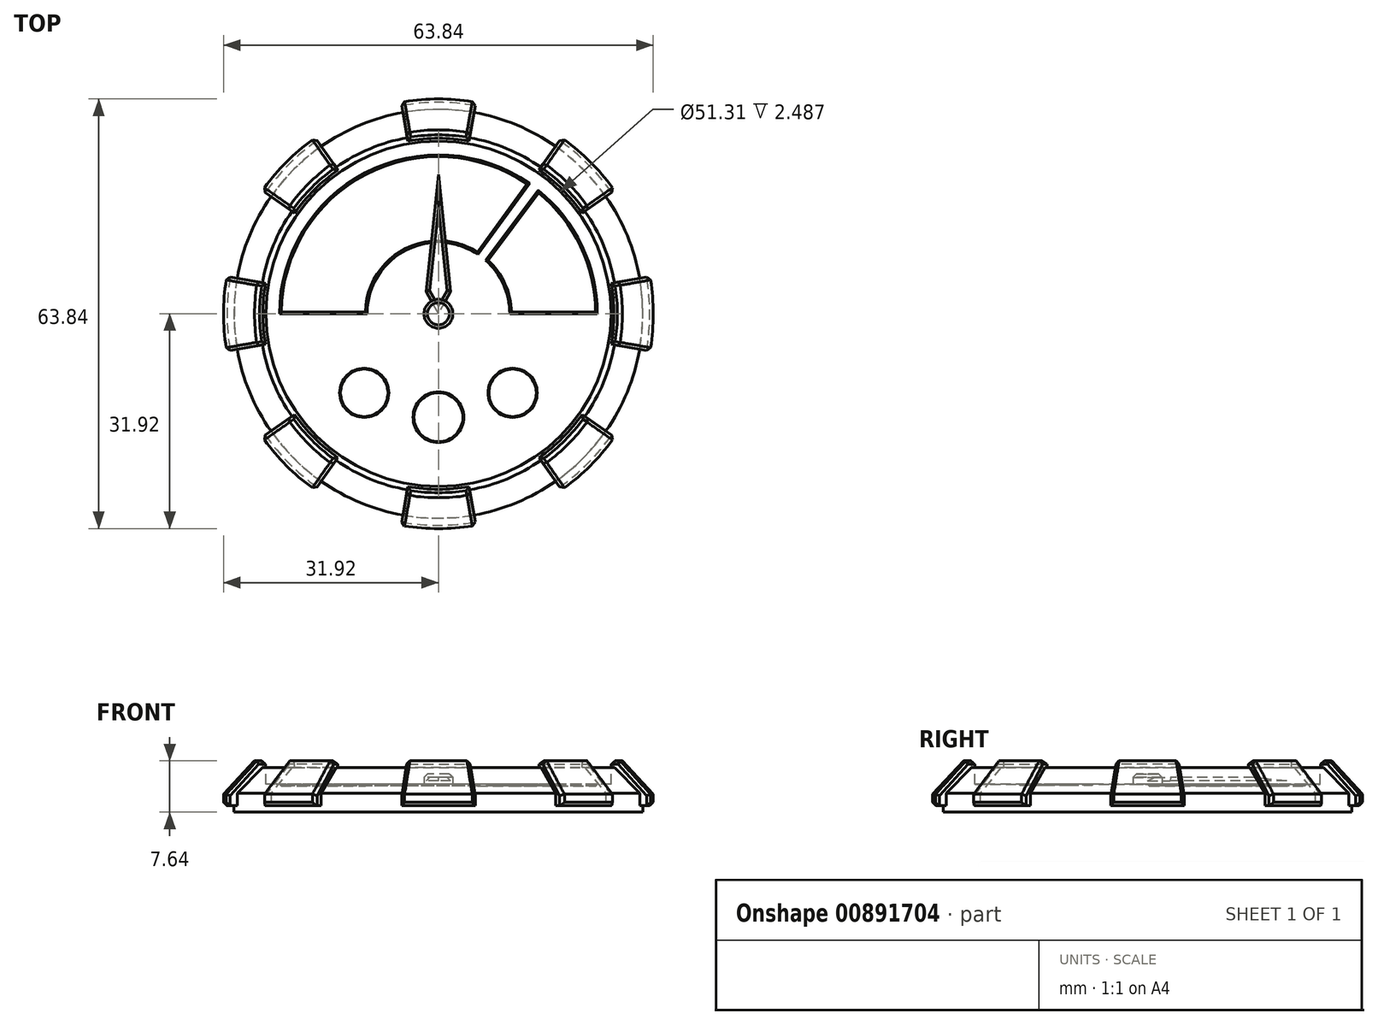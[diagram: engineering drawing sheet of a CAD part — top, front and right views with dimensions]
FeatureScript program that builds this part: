
annotation { "Feature Type Name" : "Feature", "Feature Type Description" : "" }
export const myFeature = defineFeature(function(context is Context, id is Id, definition is map)
    precondition{}
    {
        {
            var Q0;
            Q0=qCreatedBy(makeId("Top.planeOp"),FACE);
            var sketch = newSketch(context, id + "F0", { "sketchPlane" : qUnion([Q0])});
            skCircle(sketch, "E0", {"center": v(0, 0) * mm, "radius": 30.37 * mm});
            skSolve(sketch);
        }
        {
            var Q0;
            Q0 = qSketchRegion(id + "F0", true);
            extrude(context, id + "F1", {"entities" : qUnion([Q0]), "depth" : 6.65 * mm, "offsetDistance" : 25.4 * mm});
        }
        {
            var Q0;
            Q0=makeQuery(id+"F1.opExtrude","CAP_EDGE",EDGE,{"disambiguationData":[OSD([sQuery(id+"F0.wireOp",EDGE,"E0")])],"isStart":false});
            chamfer(context, id + "F2", {"entities" : qUnion([Q0]), "width" : 3.8 * mm, "tangentPropagation" : true});
        }
        {
            var Q0;
            Q0=makeQuery(id+"F1.opExtrude","CAP_FACE",FACE,{"disambiguationData":[OSD([sQuery(id+"F0.wireOp",EDGE,"E0")])],"isStart":false});
            var sketch = newSketch(context, id + "F3", { "sketchPlane" : qUnion([Q0])});
            skCircle(sketch, "E1", {"center": v(0, 0) * mm, "radius": 25.66 * mm});
            skSolve(sketch);
        }
        {
            var Q0;
            Q0 = qSketchRegion(id + "F3", true);
            extrude(context, id + "F4", {"entities" : qUnion([Q0]), "operationType" : NewBodyOperationType.REMOVE, "oppositeDirection" : true, "depth" : 2.5 * mm, "offsetDistance" : 25.4 * mm});
        }
        {
            var Q0;
            Q0=qCreatedBy(makeId("Right.planeOp"),FACE);
            var sketch = newSketch(context, id + "F5", { "sketchPlane" : qUnion([Q0])});
            skLineSegment(sketch, "E2", {"start": v(-26.08, 6.1) * mm, "end": v(-26.08, 7.63) * mm});
            skLineSegment(sketch, "E3", {"start": v(-26.08, 7.63) * mm, "end": v(-27.33, 7.63) * mm});
            skLineSegment(sketch, "E4", {"start": v(-27.33, 7.63) * mm, "end": v(-31.92, 2.66) * mm});
            skLineSegment(sketch, "E5", {"start": v(-31.92, 2.66) * mm, "end": v(-31.92, 0.95) * mm});
            skLineSegment(sketch, "E6", {"start": v(-31.92, 0.95) * mm, "end": v(-30.03, 0.95) * mm});
            skLineSegment(sketch, "E7", {"start": v(-30.03, 0.95) * mm, "end": v(-26.08, 6.1) * mm});
            skLineSegment(sketch, "E8", {"start": v(0, 11.9) * mm, "end": v(0, 0) * mm});
            skSolve(sketch);
        }
        {
            var Q0;
            Q0=makeQuery(id+"F5.imprint","IMPRINT",FACE,{"disambiguationData":[TD([[makeQuery(id+"F5.imprint","IMPRINT",EDGE,{"derivedFrom":sQuery(id+"F5.wireOp",EDGE,"E2")}),1.0]])]});
            var Q1;
            Q1=sQuery(id+"F5.wireOp",EDGE,"E8");
            revolve(context, id + "F6", {"operationType" : NewBodyOperationType.ADD, "surfaceOperationType" : NewSurfaceOperationType.NEW, "entities" : qUnion([Q0]), "axis" : qUnion([Q1]), "revolveType" : RevolveType.SYMMETRIC, "angle" : 20 * degree});
        }
        {
            var Q0;
            Q0=makeQuery(id+"F6.opRevolve","SWEPT_EDGE",EDGE,{"disambiguationData":[OSD([sQuery(id+"F5.wireOp",EDGE,"E5"),sQuery(id+"F5.wireOp",EDGE,"E6")])]});
            var Q1;
            Q1=makeQuery(id+"F6.opRevolve","CAP_EDGE",EDGE,{"disambiguationData":[OSD([sQuery(id+"F5.wireOp",EDGE,"E5")])],"isStart":false});
            var Q2;
            Q2=makeQuery(id+"F6.opRevolve","CAP_EDGE",EDGE,{"disambiguationData":[OSD([sQuery(id+"F5.wireOp",EDGE,"E4")])],"isStart":false});
            var Q3;
            Q3=makeQuery(id+"F6.opRevolve","CAP_EDGE",EDGE,{"disambiguationData":[OSD([sQuery(id+"F5.wireOp",EDGE,"E3")])],"isStart":false});
            var Q4;
            Q4=makeQuery(id+"F6.opRevolve","SWEPT_EDGE",EDGE,{"disambiguationData":[OSD([sQuery(id+"F5.wireOp",EDGE,"E2"),sQuery(id+"F5.wireOp",EDGE,"E3")])]});
            var Q5;
            Q5=makeQuery(id+"F6.opRevolve","CAP_EDGE",EDGE,{"disambiguationData":[OSD([sQuery(id+"F5.wireOp",EDGE,"E3")])],"isStart":true});
            var Q6;
            Q6=makeQuery(id+"F6.opRevolve","CAP_EDGE",EDGE,{"disambiguationData":[OSD([sQuery(id+"F5.wireOp",EDGE,"E4")])],"isStart":true});
            var Q7;
            Q7=makeQuery(id+"F6.opRevolve","CAP_EDGE",EDGE,{"disambiguationData":[OSD([sQuery(id+"F5.wireOp",EDGE,"E5")])],"isStart":true});
            chamfer(context, id + "F7", {"entities" : qUnion([Q0, Q1, Q2, Q3, Q4, Q5, Q6, Q7]), "width" : 0.5 * mm, "tangentPropagation" : true});
        }
        {
            var Q0;
            Q0=makeQuery(id+"F1.opExtrude","SWEPT_BODY",BODY,{"disambiguationData":[OSD([sQuery(id+"F0.wireOp",EDGE,"E0")])]});
            var Q1;
            Q1=sQuery(id+"F5.wireOp",EDGE,"E8");
            circularPattern(context, id + "F8", {"operationType" : NewBodyOperationType.ADD, "entities" : qUnion([Q0]), "axis" : qUnion([Q1]), "angle" : 360 * degree, "instanceCount" : 8, "equalSpace" : true});
        }
        {
            var Q0;
            Q0=makeQuery(id+"F4.boolean.opBoolean","COPY",FACE,{"derivedFrom":makeQuery(id+"F4.opExtrude","CAP_FACE",FACE,{"disambiguationData":[OSD([sQuery(id+"F3.wireOp",EDGE,"E1")])],"isStart":false})});
            var sketch = newSketch(context, id + "F9", { "sketchPlane" : qUnion([Q0])});
            skCircle(sketch, "E9", {"center": v(0, -15.36) * mm, "radius": 3.9 * mm});
            skCircle(sketch, "E10", {"center": v(11.02, -11.74) * mm, "radius": 3.78 * mm});
            skLineSegment(sketch, "E11", {"start": v(0, -8.23) * mm, "end": v(0, 0) * mm});
            skCircle(sketch, "E12.MirrorC", {"center": v(-11.02, -11.74) * mm, "radius": 3.78 * mm});
            skSolve(sketch);
        }
        {
            var Q0;
            Q0 = qSketchRegion(id + "F9", true);
            extrude(context, id + "F10", {"entities" : qUnion([Q0]), "operationType" : NewBodyOperationType.REMOVE, "oppositeDirection" : true, "depth" : 0.13 * mm, "offsetDistance" : 25.4 * mm});
        }
        {
            var Q0;
            Q0=makeQuery(id+"F4.boolean.opBoolean","COPY",FACE,{"derivedFrom":makeQuery(id+"F4.opExtrude","CAP_FACE",FACE,{"disambiguationData":[OSD([sQuery(id+"F3.wireOp",EDGE,"E1")])],"isStart":false})});
            var sketch = newSketch(context, id + "F11", { "sketchPlane" : qUnion([Q0])});
            skArc(sketch, "E13", {"start": v(23.61, 0.01) * mm, "mid": v(21.3, 10.18) * mm, "end": v(14.85, 18.36) * mm});
            skLineSegment(sketch, "E14", {"start": v(-23.61, 0.04) * mm, "end": v(-10.6, 0.04) * mm});
            skArc(sketch, "E15", {"start": v(10.6, 0.01) * mm, "mid": v(9.67, 4.36) * mm, "end": v(7.03, 7.94) * mm});
            skLineSegment(sketch, "E16", {"start": v(13.53, 19.35) * mm, "end": v(5.88, 8.82) * mm});
            skLineSegment(sketch, "E17", {"start": v(14.85, 18.36) * mm, "end": v(7.03, 7.94) * mm});
            skLineSegment(sketch, "E18", {"start": v(10.6, 0.01) * mm, "end": v(23.61, 0.01) * mm});
            skArc(sketch, "E19.trimOffspring", {"start": v(5.88, 8.82) * mm, "mid": v(-4.99, 9.36) * mm, "end": v(-10.6, 0.04) * mm});
            skArc(sketch, "E20.trimOffspring", {"start": v(13.53, 19.35) * mm, "mid": v(-10.9, 20.95) * mm, "end": v(-23.61, 0.04) * mm});
            skSolve(sketch);
        }
        {
            var Q0;
            Q0 = qSketchRegion(id + "F11", true);
            extrude(context, id + "F12", {"entities" : qUnion([Q0]), "operationType" : NewBodyOperationType.REMOVE, "oppositeDirection" : true, "depth" : 0.25 * mm, "offsetDistance" : 25.4 * mm});
        }
        {
            var Q0;
            Q0=makeQuery(id+"F4.boolean.opBoolean","COPY",FACE,{"derivedFrom":makeQuery(id+"F4.opExtrude","CAP_FACE",FACE,{"disambiguationData":[OSD([sQuery(id+"F3.wireOp",EDGE,"E1")])],"isStart":false})});
            var sketch = newSketch(context, id + "F13", { "sketchPlane" : qUnion([Q0])});
            skCircle(sketch, "E21", {"center": v(0, 0) * mm, "radius": 2.14 * mm});
            skSolve(sketch);
        }
        {
            var Q0;
            Q0 = qSketchRegion(id + "F13", true);
            extrude(context, id + "F14", {"entities" : qUnion([Q0]), "operationType" : NewBodyOperationType.ADD, "depth" : 0.5 * mm, "offsetDistance" : 25.4 * mm});
        }
        {
            var Q0;
            Q0=makeQuery(id+"F14.opExtrude","CAP_FACE",FACE,{"disambiguationData":[OSD([sQuery(id+"F13.wireOp",EDGE,"E21")])],"isStart":false});
            var sketch = newSketch(context, id + "F15", { "sketchPlane" : qUnion([Q0])});
            skSolve(sketch);
        }
        {
            var Q0;
            Q0=makeQuery(id+"F15.imprint","IMPRINT",FACE,{"disambiguationData":[TD([[makeQuery(id+"F15.imprint","IMPRINT",EDGE,{"derivedFrom":makeQuery(id+"F14.opExtrude","CAP_EDGE",EDGE,{"disambiguationData":[OSD([sQuery(id+"F13.wireOp",EDGE,"E21")])],"isStart":false})}),1.0]])]});
            extrude(context, id + "F16", {"entities" : qUnion([Q0]), "operationType" : NewBodyOperationType.ADD, "depth" : 1.02 * mm, "offsetDistance" : 25.4 * mm});
        }
        {
            var Q0;
            Q0=makeQuery(id+"F10.boolean.opBoolean","COPY",EDGE,{"derivedFrom":makeQuery(id+"F10.opExtrude","CAP_EDGE",EDGE,{"disambiguationData":[OSD([sQuery(id+"F9.wireOp",EDGE,"E12.MirrorC")])],"isStart":false})});
            var Q1;
            Q1=makeQuery(id+"F10.boolean.opBoolean","COPY",EDGE,{"derivedFrom":makeQuery(id+"F10.opExtrude","CAP_EDGE",EDGE,{"disambiguationData":[OSD([sQuery(id+"F9.wireOp",EDGE,"E9")])],"isStart":false})});
            var Q2;
            Q2=makeQuery(id+"F10.boolean.opBoolean","COPY",EDGE,{"derivedFrom":makeQuery(id+"F10.opExtrude","CAP_EDGE",EDGE,{"disambiguationData":[OSD([sQuery(id+"F9.wireOp",EDGE,"E10")])],"isStart":false})});
            var Q3;
            Q3=makeQuery(id+"F12.boolean.opBoolean","COPY",EDGE,{"derivedFrom":makeQuery(id+"F12.opExtrude","CAP_EDGE",EDGE,{"disambiguationData":[OSD([sQuery(id+"F11.wireOp",EDGE,"E20.trimOffspring")])],"isStart":false})});
            var Q4;
            Q4=makeQuery(id+"F12.boolean.opBoolean","COPY",EDGE,{"derivedFrom":makeQuery(id+"F12.opExtrude","CAP_EDGE",EDGE,{"disambiguationData":[OSD([sQuery(id+"F11.wireOp",EDGE,"E14")])],"isStart":false})});
            var Q5;
            Q5=makeQuery(id+"F12.boolean.opBoolean","COPY",EDGE,{"derivedFrom":makeQuery(id+"F12.opExtrude","CAP_EDGE",EDGE,{"disambiguationData":[OSD([sQuery(id+"F11.wireOp",EDGE,"E19.trimOffspring")])],"isStart":false})});
            var Q6;
            Q6=makeQuery(id+"F12.boolean.opBoolean","COPY",EDGE,{"derivedFrom":makeQuery(id+"F12.opExtrude","CAP_EDGE",EDGE,{"disambiguationData":[OSD([sQuery(id+"F11.wireOp",EDGE,"E16")])],"isStart":false})});
            var Q7;
            Q7=makeQuery(id+"F12.boolean.opBoolean","COPY",EDGE,{"derivedFrom":makeQuery(id+"F12.opExtrude","CAP_EDGE",EDGE,{"disambiguationData":[OSD([sQuery(id+"F11.wireOp",EDGE,"E18")])],"isStart":false})});
            var Q8;
            Q8=makeQuery(id+"F12.boolean.opBoolean","COPY",EDGE,{"derivedFrom":makeQuery(id+"F12.opExtrude","CAP_EDGE",EDGE,{"disambiguationData":[OSD([sQuery(id+"F11.wireOp",EDGE,"E13")])],"isStart":false})});
            var Q9;
            Q9=makeQuery(id+"F12.boolean.opBoolean","COPY",EDGE,{"derivedFrom":makeQuery(id+"F12.opExtrude","CAP_EDGE",EDGE,{"disambiguationData":[OSD([sQuery(id+"F11.wireOp",EDGE,"E15")])],"isStart":false})});
            var Q10;
            Q10=makeQuery(id+"F12.boolean.opBoolean","COPY",EDGE,{"derivedFrom":makeQuery(id+"F12.opExtrude","CAP_EDGE",EDGE,{"disambiguationData":[OSD([sQuery(id+"F11.wireOp",EDGE,"E17")])],"isStart":false})});
            chamfer(context, id + "F17", {"entities" : qUnion([Q0, Q1, Q2, Q3, Q4, Q5, Q6, Q7, Q8, Q9, Q10]), "width" : 0.25 * mm, "tangentPropagation" : true});
        }
        {
            var Q0;
            Q0=makeQuery(id+"F4.boolean.opBoolean","COPY",FACE,{"derivedFrom":makeQuery(id+"F4.opExtrude","CAP_FACE",FACE,{"disambiguationData":[OSD([sQuery(id+"F3.wireOp",EDGE,"E1")])],"isStart":false})});
            var sketch = newSketch(context, id + "F18", { "sketchPlane" : qUnion([Q0])});
            skLineSegment(sketch, "E22", {"start": v(0, 0) * mm, "end": v(0, 20.68) * mm});
            skLineSegment(sketch, "E23", {"start": v(0, 20.68) * mm, "end": v(1.8, 3.33) * mm});
            skLineSegment(sketch, "E24", {"start": v(1.8, 3.33) * mm, "end": v(0, 0) * mm});
            skLineSegment(sketch, "E25.MirrorCS", {"start": v(0, 20.68) * mm, "end": v(-1.8, 3.33) * mm});
            skLineSegment(sketch, "E26.MirrorCS", {"start": v(-1.8, 3.33) * mm, "end": v(0, 0) * mm});
            skSolve(sketch);
        }
        {
            var Q0;
            Q0 = qSketchRegion(id + "F18", true);
            extrude(context, id + "F19", {"entities" : qUnion([Q0]), "depth" : 0.5 * mm, "offsetDistance" : 25.4 * mm, "hasDraft" : true, "draftAngle" : 45 * degree, "draftPullDirection" : true});
        }
        {
            var Q0;
            Q0=makeQuery(id+"F19.opExtrude","SWEPT_BODY",BODY,{"disambiguationData":[OSD([sQuery(id+"F18.wireOp",EDGE,"E23"),sQuery(id+"F18.wireOp",EDGE,"E24"),sQuery(id+"F18.wireOp",EDGE,"E25.MirrorCS"),sQuery(id+"F18.wireOp",EDGE,"E26.MirrorCS")])]});
            transform(context, id + "F20", {"entities" : qUnion([Q0]), "transformType" : TransformType.TRANSLATION_3D, "dx" : 0 * mm, "dy" : 0 * mm, "dz" : 0.48 * mm, "makeCopy" : false});
        }
        {
            var Q0;
            Q0=makeQuery(id+"F16.opExtrude","CAP_EDGE",EDGE,{"disambiguationData":[OSD([sQuery(id+"F13.wireOp",EDGE,"E21")])],"isStart":false});
            chamfer(context, id + "F21", {"entities" : qUnion([Q0]), "width" : 0.5 * mm, "tangentPropagation" : true});
        }
    });
